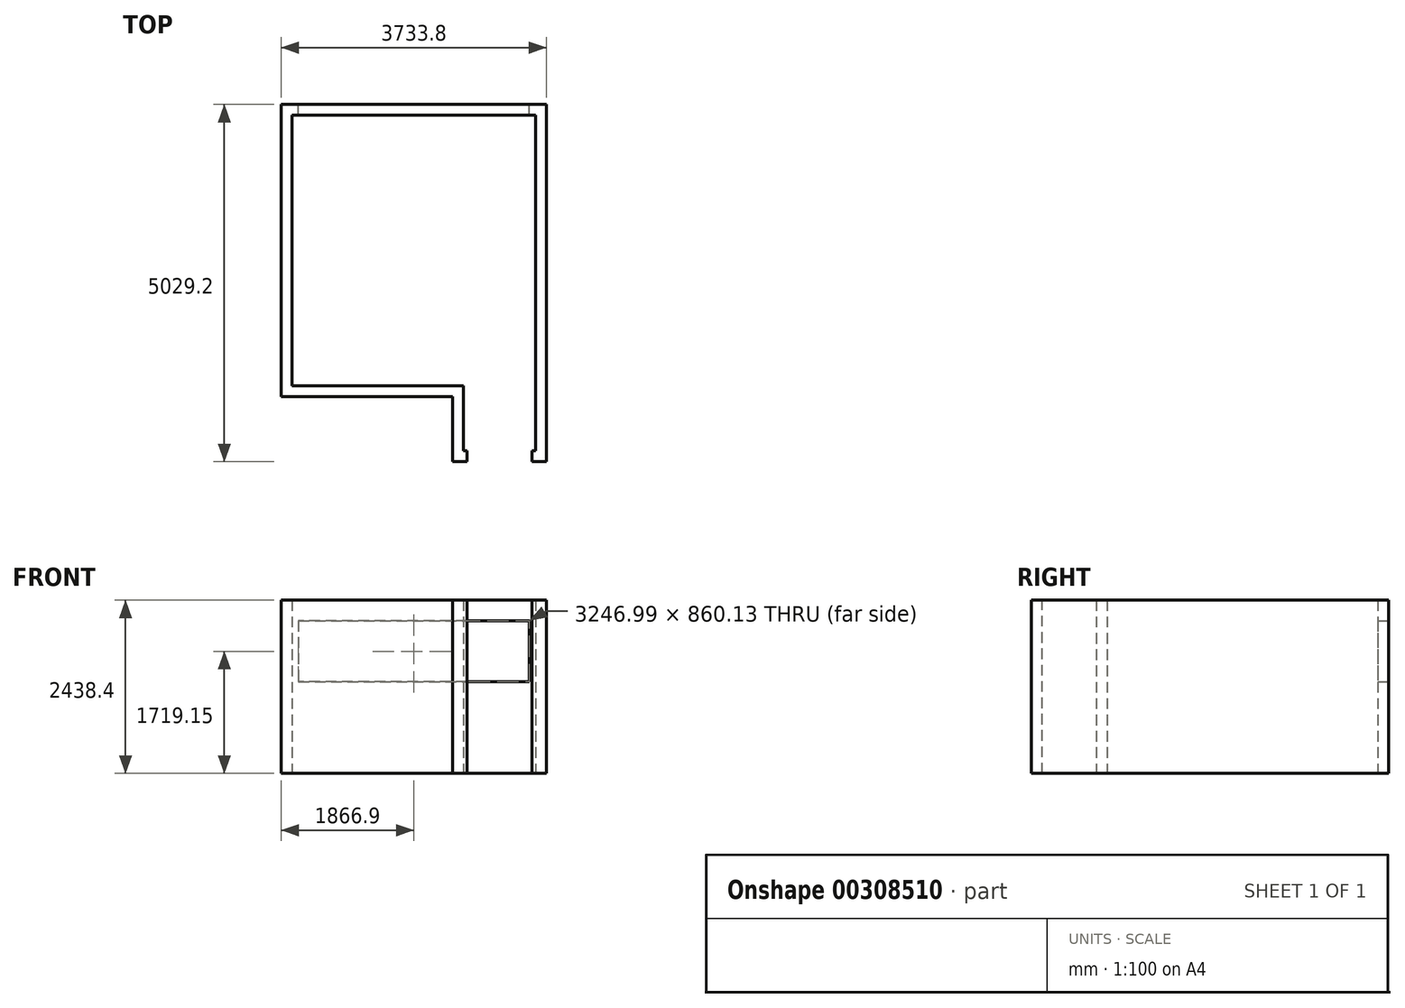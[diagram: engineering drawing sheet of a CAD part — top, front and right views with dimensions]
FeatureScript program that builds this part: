
annotation { "Feature Type Name" : "Feature", "Feature Type Description" : "" }
export const myFeature = defineFeature(function(context is Context, id is Id, definition is map)
    precondition{}
    {
        {
            var Q0;
            Q0=qCreatedBy(makeId("Top.planeOp"),FACE);
            var sketch = newSketch(context, id + "F0", { "sketchPlane" : qUnion([Q0])});
            skLineSegment(sketch, "E0.bottom", {"start": v(1714.5, -2362.2) * mm, "end": v(698.5, -2362.2) * mm});
            skLineSegment(sketch, "E0.top", {"start": v(1714.5, 2362.2) * mm, "end": v(-1714.5, 2362.2) * mm});
            skLineSegment(sketch, "E0.left", {"start": v(1714.5, -2362.2) * mm, "end": v(1714.5, 2362.2) * mm});
            skLineSegment(sketch, "E0.right", {"start": v(-1714.5, -1447.8) * mm, "end": v(-1714.5, 2362.2) * mm});
            skPoint(sketch, "E0.middle", {"position": v(0, 0) * mm});
            skLineSegment(sketch, "E1", {"start": v(698.5, -2362.2) * mm, "end": v(698.5, -1447.8) * mm});
            skLineSegment(sketch, "E2", {"start": v(698.5, -1447.8) * mm, "end": v(-1714.5, -1447.8) * mm});
            skLineSegment(sketch, "E3.0", {"start": v(546.1, -1600.2) * mm, "end": v(-1866.9, -1600.2) * mm});
            skLineSegment(sketch, "E3.1", {"start": v(1866.9, 2514.6) * mm, "end": v(-1866.9, 2514.6) * mm});
            skLineSegment(sketch, "E3.2", {"start": v(1866.9, -2514.6) * mm, "end": v(1866.9, 2514.6) * mm});
            skLineSegment(sketch, "E3.3", {"start": v(-1866.9, -1600.2) * mm, "end": v(-1866.9, 2514.6) * mm});
            skLineSegment(sketch, "E3.4", {"start": v(1866.9, -2514.6) * mm, "end": v(546.1, -2514.6) * mm});
            skLineSegment(sketch, "E3.5", {"start": v(546.1, -2514.6) * mm, "end": v(546.1, -1600.2) * mm});
            skSolve(sketch);
        }
        {
            var Q0;
            Q0=makeQuery(id+"F0.imprint","IMPRINT",FACE,{"disambiguationData":[TD([[makeQuery(id+"F0.imprint","IMPRINT",EDGE,{"derivedFrom":sQuery(id+"F0.wireOp",EDGE,"E0.bottom")}),1.0]])]});
            extrude(context, id + "F1", {"entities" : qUnion([Q0]), "depth" : 2438.4 * mm});
        }
        {
            var Q0;
            Q0=makeQuery(id+"F1.opExtrude","SWEPT_FACE",FACE,{"disambiguationData":[OSD([sQuery(id+"F0.wireOp",EDGE,"E3.4")])]});
            var sketch = newSketch(context, id + "F2", { "sketchPlane" : qUnion([Q0])});
            skLineSegment(sketch, "E4.bottom", {"start": v(1663.7, -777.66) * mm, "end": v(749.3, -777.66) * mm});
            skLineSegment(sketch, "E4.top", {"start": v(1663.7, 3531.71) * mm, "end": v(749.3, 3531.71) * mm});
            skLineSegment(sketch, "E4.left", {"start": v(1663.7, -777.66) * mm, "end": v(1663.7, 3531.71) * mm});
            skLineSegment(sketch, "E4.right", {"start": v(749.3, -777.66) * mm, "end": v(749.3, 3531.71) * mm});
            skPoint(sketch, "E4.middle", {"position": v(1206.5, 1377.03) * mm});
            skSolve(sketch);
        }
        {
            var Q0;
            Q0 = qSketchRegion(id + "F2", true);
            extrude(context, id + "F3", {"entities" : qUnion([Q0]), "operationType" : NewBodyOperationType.REMOVE, "oppositeDirection" : true, "depth" : 406.4 * mm});
        }
        {
            var Q0;
            Q0=makeQuery(id+"F1.opExtrude","SWEPT_FACE",FACE,{"disambiguationData":[OSD([sQuery(id+"F0.wireOp",EDGE,"E3.1")])]});
            var sketch = newSketch(context, id + "F4", { "sketchPlane" : qUnion([Q0])});
            skLineSegment(sketch, "E5.bottom", {"start": v(1623.5, 1289.09) * mm, "end": v(-1623.5, 1289.09) * mm});
            skLineSegment(sketch, "E5.top", {"start": v(1623.5, 2149.21) * mm, "end": v(-1623.5, 2149.21) * mm});
            skLineSegment(sketch, "E5.left", {"start": v(1623.5, 1289.09) * mm, "end": v(1623.5, 2149.21) * mm});
            skLineSegment(sketch, "E5.right", {"start": v(-1623.5, 1289.09) * mm, "end": v(-1623.5, 2149.21) * mm});
            skPoint(sketch, "E5.middle", {"position": v(0, 1719.15) * mm});
            skPoint(sketch, "E5.middle.positionSnap0", {"position": v(0, 2438.4) * mm});
            skPoint(sketch, "E5.centerSnap0", {"position": v(0, 2438.4) * mm});
            skSolve(sketch);
        }
        {
            var Q0;
            Q0 = qSketchRegion(id + "F4", true);
            extrude(context, id + "F5", {"entities" : qUnion([Q0]), "operationType" : NewBodyOperationType.REMOVE, "oppositeDirection" : true, "depth" : 482.6 * mm});
        }
    });
